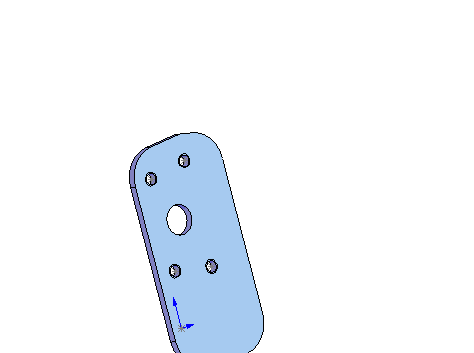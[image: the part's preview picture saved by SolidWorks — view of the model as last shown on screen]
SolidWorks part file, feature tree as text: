
SOLIDWORKS PART (.sldprt)
format: sldprt  version: not decoded by parser v0  size: 179,712 bytes
history: native  units: mm
features: sketch x5, thread x4, plane x3, material x1, extrude x1, cut_extrude x1, fillet x1, hole x1 + 1 further entry (+7 scaffold rows collapsed)
feature tree (25):
  scaffold x7  (default folders/planes/origin — collapsed)
  material  "Matériau <non spécifié>"
  "Corps de surface"
  plane  "Face"
  plane  "Dessus"
  plane  "Droite"
  sketch  "Esquisse2"  dims[c1.D1=~46.300844mm c2.D1=95.0deg c2.D2=~52.020409mm c3.D2=100.0deg c3.D3=~131.572801mm c4.D3=95.0deg c4.D4=~47.977551mm c5.D4=95.0deg c5.D5=40.0mm c5.D6=4.0mm c5.D7=79.0mm c5.D8=78.5mm]
  extrude  "Extrusion1"  Depth=3mm
  sketch  "Esquisse3"  dims[D2=11.0mm D1=27.0mm D3=15.0mm]
  cut_extrude  "Enlèv. mat.-Extru.1"  [1 undecoded]
  fillet  "Congé1"  Radius=12mm
  sketch  "Esquisse7"  dims[c1.D1=11.0mm c1.D2=11.0mm c1.D6=11.0mm c1.D8=11.0mm c2.D1=17.0mm c2.D2=17.0mm c2.D3=19.5mm c2.D4=19.5mm c2.D5=7.5mm c2.D6=8.5mm c2.D7=8.5mm c2.D8=7.5mm]
  hole  "Trou taraudé M5x0.82"  Diameter=4.2mm Depth=3mm
  sketch  "Esquisse3D3"
  sketch  "Esquisse8"  dims[hole-wizard template sketch: 47 standard entries collapsed; hole parameters kept: c15.Profondeur du trou pour taraudage=3.0mm c15.D3=~14.816244mm c15.Angle de pointe=118.0deg]
  thread  "Représentation de filetage6"  Diameter=3mm  [1 undecoded]
  thread  "Représentation de filetage7"  Diameter=3mm  [1 undecoded]
  thread  "Représentation de filetage8"  Diameter=3mm  [1 undecoded]
  thread  "Représentation de filetage9"  Diameter=3mm  [1 undecoded]
decode coverage: 11 of 13 modeling features carry decoded parameters; 1 rows unclassified (native names shown)
note: ~ marks probable driven/reference dimensions
note: 5 parameter values undecoded
note: suppression state not decoded; provenance and decode notes live in map.json
